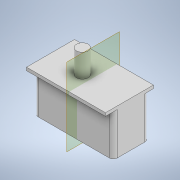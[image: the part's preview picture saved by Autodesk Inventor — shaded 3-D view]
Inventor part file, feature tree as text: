
AUTODESK INVENTOR PART (.ipt)
format: ipt  version: 2021 (Build 250183000, 183)  size: 176,640 bytes
history: native  units: in
note: dims shown in document units (in); Inventor stores cm internally (conversion verified against a paired STEP export)
features: extrude x4, sketch x4, plane x1
ambient origin geometry x8: Origin, YZ Plane, XZ Plane, XY Plane, X Axis, Y Axis, Z Axis, Center Point
bodies: Solid1 (feature_tree)
feature tree (9):
  extrude  "Extrusion1"  Depth=0.9in
  extrude  "Extrusion8"  Depth=0.1in
  extrude  "Extrusion9"  Depth=0.09in
  extrude  "Extrusion10"  Depth=0.0787in
  plane  "Work Plane1"
  sketch  "Sketch1"  dims[d0=2.0in d1=0.9in]
  sketch  "Sketch8"  dims[d2=0.1in d3=0.1in]
  sketch  "Sketch9"  dims[d4=0.09in d5=0.09in]
  sketch  "Sketch10"  dims[d6=0.7in d7=0.75in d9=0.35in d10=0.1in d11=0.1in d12=0.375in d13=0.1in d14=0.1in d15=0.1in d16=1.1417in d17=0.0in d62=0.2953in d63=0.1in d64=0.8661in d65=0.5906in d66=0.0in d67=0.315in d68=0.1575in d69=0.0984in d70=0.0984in d71=0.0591in d72=0.0in d73=0.1969in d74=0.1181in d75=0.0787in d76=0.0in]
